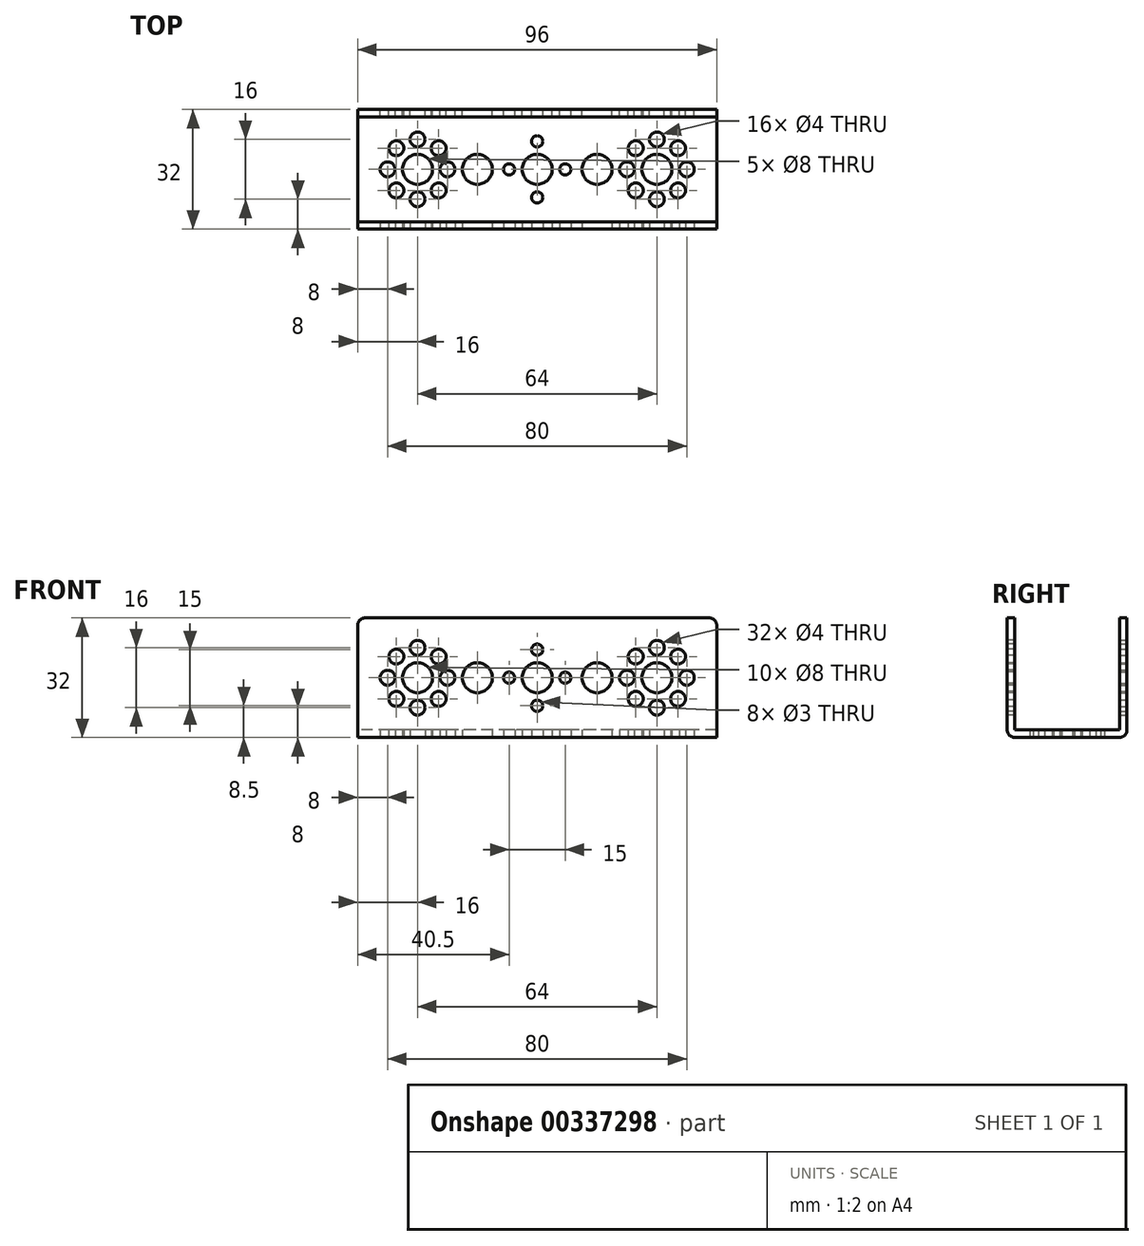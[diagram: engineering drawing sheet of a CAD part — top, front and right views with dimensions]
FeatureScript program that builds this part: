
annotation { "Feature Type Name" : "Feature", "Feature Type Description" : "" }
export const myFeature = defineFeature(function(context is Context, id is Id, definition is map)
    precondition{}
    {
        {
            var Q0;
            Q0=qCreatedBy(makeId("Top.planeOp"),FACE);
            var sketch = newSketch(context, id + "F0", { "sketchPlane" : qUnion([Q0])});
            skLineSegment(sketch, "E0.bottom", {"start": v(48, 16) * mm, "end": v(-48, 16) * mm});
            skLineSegment(sketch, "E0.top", {"start": v(48, -16) * mm, "end": v(-48, -16) * mm});
            skLineSegment(sketch, "E0.left", {"start": v(48, 16) * mm, "end": v(48, -16) * mm});
            skLineSegment(sketch, "E0.right", {"start": v(-48, 16) * mm, "end": v(-48, -16) * mm});
            skPoint(sketch, "E0.middle", {"position": v(0, 0) * mm});
            skLineSegment(sketch, "E1", {"start": v(-32, 2.64) * mm, "end": v(-32, 0) * mm});
            skLineSegment(sketch, "E2", {"start": v(-32, 0) * mm, "end": v(-32, -2.64) * mm});
            skLineSegment(sketch, "E3", {"start": v(-43.39, 0) * mm, "end": v(-32, 0) * mm});
            skLineSegment(sketch, "E4", {"start": v(-32, 0) * mm, "end": v(-37.82, 0) * mm});
            skLineSegment(sketch, "E5", {"start": v(-32, 0) * mm, "end": v(-30.72, 1.28) * mm});
            skLineSegment(sketch, "E6", {"start": v(-32, 0) * mm, "end": v(-33.4, -1.4) * mm});
            skLineSegment(sketch, "E7", {"start": v(-32, 0) * mm, "end": v(-33.4, 1.4) * mm});
            skLineSegment(sketch, "E8", {"start": v(-32, 0) * mm, "end": v(-30.62, -1.38) * mm});
            skCircle(sketch, "E9", {"center": v(-32, 0) * mm, "radius": 4 * mm});
            skCircle(sketch, "E10", {"center": v(-37.66, 5.66) * mm, "radius": 2 * mm});
            skCircle(sketch, "E11", {"center": v(-32, 8) * mm, "radius": 2 * mm});
            skCircle(sketch, "E12", {"center": v(-26.34, 5.66) * mm, "radius": 2 * mm});
            skCircle(sketch, "E13", {"center": v(-24, 0) * mm, "radius": 2 * mm});
            skCircle(sketch, "E14", {"center": v(-40, 0) * mm, "radius": 2 * mm});
            skCircle(sketch, "E15", {"center": v(-37.66, -5.66) * mm, "radius": 2 * mm});
            skCircle(sketch, "E16", {"center": v(-32, -8) * mm, "radius": 2 * mm});
            skCircle(sketch, "E17", {"center": v(-26.34, -5.66) * mm, "radius": 2 * mm});
            skCircle(sketch, "E18", {"center": v(-16, 0) * mm, "radius": 4 * mm});
            skCircle(sketch, "E19", {"center": v(0, 0) * mm, "radius": 4 * mm});
            skCircle(sketch, "E20", {"center": v(0, 7.5) * mm, "radius": 1.5 * mm});
            skCircle(sketch, "E21", {"center": v(7.5, 0) * mm, "radius": 1.5 * mm});
            skCircle(sketch, "E22", {"center": v(0, -7.5) * mm, "radius": 1.5 * mm});
            skCircle(sketch, "E23", {"center": v(-7.5, 0) * mm, "radius": 1.5 * mm});
            skCircle(sketch, "E24.MirrorC", {"center": v(16, 0) * mm, "radius": 4 * mm});
            skCircle(sketch, "E25.MirrorC", {"center": v(26.34, 5.66) * mm, "radius": 2 * mm});
            skCircle(sketch, "E26.MirrorC", {"center": v(32, 8) * mm, "radius": 2 * mm});
            skCircle(sketch, "E27.MirrorC", {"center": v(37.66, 5.66) * mm, "radius": 2 * mm});
            skCircle(sketch, "E28.MirrorC", {"center": v(37.66, -5.66) * mm, "radius": 2 * mm});
            skCircle(sketch, "E29.MirrorC", {"center": v(32, -8) * mm, "radius": 2 * mm});
            skCircle(sketch, "E30.MirrorC", {"center": v(26.34, -5.66) * mm, "radius": 2 * mm});
            skCircle(sketch, "E31.MirrorC", {"center": v(24, 0) * mm, "radius": 2 * mm});
            skCircle(sketch, "E32.MirrorC", {"center": v(32, 0) * mm, "radius": 4 * mm});
            skCircle(sketch, "E33.MirrorC", {"center": v(40, 0) * mm, "radius": 2 * mm});
            skSolve(sketch);
        }
        {
            var Q0;
            Q0=sQuery(id+"F0.wireOp",EDGE,"E0.top");
            var Q1;
            Q1=qCreatedBy(makeId("Front.planeOp"),FACE);
            cPlane(context, id + "F1", {"entities" : qUnion([Q0, Q1]), "cplaneType" : CPlaneType.LINE_ANGLE, "offset" : 25.4 * mm, "angle" : 0 * degree, "width" : 152.4 * mm, "height" : 152.4 * mm});
        }
        {
            var Q0;
            Q0=sQuery(id+"F0.wireOp",EDGE,"E0.bottom");
            var Q1;
            Q1=qCreatedBy(makeId("Front.planeOp"),FACE);
            cPlane(context, id + "F2", {"entities" : qUnion([Q0, Q1]), "cplaneType" : CPlaneType.LINE_ANGLE, "offset" : 25.4 * mm, "angle" : 0 * degree, "width" : 152.4 * mm, "height" : 152.4 * mm});
        }
        {
            var Q0;
            Q0=qCreatedBy(id+"F2.planeOp",FACE);
            var sketch = newSketch(context, id + "F3", { "sketchPlane" : qUnion([Q0])});
            skLineSegment(sketch, "E34.bottom", {"start": v(-48, 0) * mm, "end": v(48, 0) * mm});
            skLineSegment(sketch, "E34.top", {"start": v(-48, 32) * mm, "end": v(48, 32) * mm});
            skLineSegment(sketch, "E34.left", {"start": v(-48, 0) * mm, "end": v(-48, 32) * mm});
            skLineSegment(sketch, "E34.right", {"start": v(48, 0) * mm, "end": v(48, 32) * mm});
            skLineSegment(sketch, "E35", {"start": v(-32, 18.64) * mm, "end": v(-32, 16) * mm});
            skLineSegment(sketch, "E36", {"start": v(-32, 16) * mm, "end": v(-32, 13.36) * mm});
            skLineSegment(sketch, "E37", {"start": v(-45.1, 16) * mm, "end": v(-32, 16) * mm});
            skLineSegment(sketch, "E38", {"start": v(-32, 16) * mm, "end": v(-39.54, 16) * mm});
            skLineSegment(sketch, "E39", {"start": v(-32, 16) * mm, "end": v(-30.72, 17.28) * mm});
            skLineSegment(sketch, "E40", {"start": v(-32, 16) * mm, "end": v(-33.4, 14.6) * mm});
            skLineSegment(sketch, "E41", {"start": v(-32, 16) * mm, "end": v(-33.4, 17.4) * mm});
            skLineSegment(sketch, "E42", {"start": v(-32, 16) * mm, "end": v(-30.62, 14.62) * mm});
            skCircle(sketch, "E43", {"center": v(-32, 16) * mm, "radius": 4 * mm});
            skCircle(sketch, "E44", {"center": v(-37.66, 21.66) * mm, "radius": 2 * mm});
            skCircle(sketch, "E45", {"center": v(-32, 24) * mm, "radius": 2 * mm});
            skCircle(sketch, "E46", {"center": v(-26.34, 21.66) * mm, "radius": 2 * mm});
            skCircle(sketch, "E47", {"center": v(-24, 16) * mm, "radius": 2 * mm});
            skCircle(sketch, "E48", {"center": v(-40, 16) * mm, "radius": 2 * mm});
            skCircle(sketch, "E49", {"center": v(-37.66, 10.34) * mm, "radius": 2 * mm});
            skCircle(sketch, "E50", {"center": v(-32, 8) * mm, "radius": 2 * mm});
            skCircle(sketch, "E51", {"center": v(-26.34, 10.34) * mm, "radius": 2 * mm});
            skPoint(sketch, "E52", {"position": v(-48, 16) * mm});
            skCircle(sketch, "E53", {"center": v(0, 16) * mm, "radius": 4 * mm});
            skCircle(sketch, "E54", {"center": v(-16, 16) * mm, "radius": 4 * mm});
            skCircle(sketch, "E55", {"center": v(-7.5, 16) * mm, "radius": 1.5 * mm});
            skCircle(sketch, "E56", {"center": v(0, 23.5) * mm, "radius": 1.5 * mm});
            skCircle(sketch, "E57", {"center": v(7.5, 16) * mm, "radius": 1.5 * mm});
            skCircle(sketch, "E58", {"center": v(0, 8.5) * mm, "radius": 1.5 * mm});
            skCircle(sketch, "E59.MirrorC", {"center": v(16, 16) * mm, "radius": 4 * mm});
            skCircle(sketch, "E60.MirrorC", {"center": v(26.34, 21.66) * mm, "radius": 2 * mm});
            skCircle(sketch, "E61.MirrorC", {"center": v(32, 24) * mm, "radius": 2 * mm});
            skCircle(sketch, "E62.MirrorC", {"center": v(37.66, 21.66) * mm, "radius": 2 * mm});
            skCircle(sketch, "E63.MirrorC", {"center": v(40, 16) * mm, "radius": 2 * mm});
            skCircle(sketch, "E64.MirrorC", {"center": v(37.66, 10.34) * mm, "radius": 2 * mm});
            skCircle(sketch, "E65.MirrorC", {"center": v(32, 8) * mm, "radius": 2 * mm});
            skCircle(sketch, "E66.MirrorC", {"center": v(26.34, 10.34) * mm, "radius": 2 * mm});
            skCircle(sketch, "E67.MirrorC", {"center": v(24, 16) * mm, "radius": 2 * mm});
            skCircle(sketch, "E68.MirrorC", {"center": v(32, 16) * mm, "radius": 4 * mm});
            skSolve(sketch);
        }
        {
            var Q0;
            Q0=qCreatedBy(id+"F1.planeOp",FACE);
            var sketch = newSketch(context, id + "F4", { "sketchPlane" : qUnion([Q0])});
            skLineSegment(sketch, "E69.bottom", {"start": v(48, 0) * mm, "end": v(-48, 0) * mm});
            skLineSegment(sketch, "E69.top", {"start": v(48, 32) * mm, "end": v(-48, 32) * mm});
            skLineSegment(sketch, "E69.left", {"start": v(48, 0) * mm, "end": v(48, 32) * mm});
            skLineSegment(sketch, "E69.right", {"start": v(-48, 0) * mm, "end": v(-48, 32) * mm});
            skLineSegment(sketch, "E70", {"start": v(-32, 18.64) * mm, "end": v(-32, 16) * mm});
            skLineSegment(sketch, "E71", {"start": v(-32, 16) * mm, "end": v(-32, 13.36) * mm});
            skLineSegment(sketch, "E72", {"start": v(-32, 16) * mm, "end": v(-39.54, 16) * mm});
            skLineSegment(sketch, "E73", {"start": v(-32, 16) * mm, "end": v(-30.72, 17.28) * mm});
            skLineSegment(sketch, "E74", {"start": v(-32, 16) * mm, "end": v(-33.4, 14.6) * mm});
            skLineSegment(sketch, "E75", {"start": v(-32, 16) * mm, "end": v(-33.4, 17.4) * mm});
            skLineSegment(sketch, "E76", {"start": v(-32, 16) * mm, "end": v(-30.62, 14.62) * mm});
            skCircle(sketch, "E77", {"center": v(-32, 16) * mm, "radius": 4 * mm});
            skCircle(sketch, "E78", {"center": v(-37.66, 21.66) * mm, "radius": 2 * mm});
            skCircle(sketch, "E79", {"center": v(-32, 24) * mm, "radius": 2 * mm});
            skCircle(sketch, "E80", {"center": v(-26.34, 21.66) * mm, "radius": 2 * mm});
            skCircle(sketch, "E81", {"center": v(-24, 16) * mm, "radius": 2 * mm});
            skCircle(sketch, "E82", {"center": v(-40, 16) * mm, "radius": 2 * mm});
            skCircle(sketch, "E83", {"center": v(-37.66, 10.34) * mm, "radius": 2 * mm});
            skCircle(sketch, "E84", {"center": v(-32, 8) * mm, "radius": 2 * mm});
            skCircle(sketch, "E85", {"center": v(-26.34, 10.34) * mm, "radius": 2 * mm});
            skCircle(sketch, "E86", {"center": v(0, 16) * mm, "radius": 4 * mm});
            skCircle(sketch, "E87", {"center": v(-16, 16) * mm, "radius": 4 * mm});
            skCircle(sketch, "E88", {"center": v(-7.5, 16) * mm, "radius": 1.5 * mm});
            skCircle(sketch, "E89", {"center": v(0, 23.5) * mm, "radius": 1.5 * mm});
            skCircle(sketch, "E90", {"center": v(7.5, 16) * mm, "radius": 1.5 * mm});
            skCircle(sketch, "E91", {"center": v(0, 8.5) * mm, "radius": 1.5 * mm});
            skPoint(sketch, "E92", {"position": v(48, 16) * mm});
            skCircle(sketch, "E93.MirrorC", {"center": v(16, 16) * mm, "radius": 4 * mm});
            skCircle(sketch, "E94.MirrorC", {"center": v(24, 16) * mm, "radius": 2 * mm});
            skCircle(sketch, "E95.MirrorC", {"center": v(26.34, 21.66) * mm, "radius": 2 * mm});
            skCircle(sketch, "E96.MirrorC", {"center": v(32, 24) * mm, "radius": 2 * mm});
            skCircle(sketch, "E97.MirrorC", {"center": v(37.66, 21.66) * mm, "radius": 2 * mm});
            skCircle(sketch, "E98.MirrorC", {"center": v(40, 16) * mm, "radius": 2 * mm});
            skCircle(sketch, "E99.MirrorC", {"center": v(37.66, 10.34) * mm, "radius": 2 * mm});
            skCircle(sketch, "E100.MirrorC", {"center": v(32, 8) * mm, "radius": 2 * mm});
            skCircle(sketch, "E101.MirrorC", {"center": v(26.34, 10.34) * mm, "radius": 2 * mm});
            skCircle(sketch, "E102.MirrorC", {"center": v(32, 16) * mm, "radius": 4 * mm});
            skSolve(sketch);
        }
        {
            var Q0;
            Q0=makeQuery(id+"F0.imprint","IMPRINT",FACE,{"disambiguationData":[TD([[makeQuery(id+"F0.imprint","IMPRINT",EDGE,{"derivedFrom":sQuery(id+"F0.wireOp",EDGE,"E0.bottom")}),1.0]])]});
            extrude(context, id + "F5", {"entities" : qUnion([Q0]), "depth" : 2 * mm});
        }
        {
            var Q0;
            Q0=makeQuery(id+"F3.imprint","IMPRINT",FACE,{"disambiguationData":[TD([[makeQuery(id+"F3.imprint","IMPRINT",EDGE,{"derivedFrom":sQuery(id+"F3.wireOp",EDGE,"E34.bottom")}),1.0]])]});
            extrude(context, id + "F6", {"entities" : qUnion([Q0]), "operationType" : NewBodyOperationType.ADD, "oppositeDirection" : true, "depth" : 2 * mm});
        }
        {
            var Q0;
            Q0=makeQuery(id+"F4.imprint","IMPRINT",FACE,{"disambiguationData":[TD([[makeQuery(id+"F4.imprint","IMPRINT",EDGE,{"derivedFrom":sQuery(id+"F4.wireOp",EDGE,"E69.bottom")}),-1.0]])]});
            extrude(context, id + "F7", {"entities" : qUnion([Q0]), "operationType" : NewBodyOperationType.ADD, "depth" : 2 * mm});
        }
        {
            var Q0;
            Q0=makeQuery(id+"F5.opExtrude","CAP_EDGE",EDGE,{"disambiguationData":[OSD([sQuery(id+"F0.wireOp",EDGE,"E0.bottom")])],"isStart":true});
            var Q1;
            Q1=makeQuery(id+"F6.opExtrude","SWEPT_EDGE",EDGE,{"disambiguationData":[OSD([sQuery(id+"F3.wireOp",EDGE,"E34.top"),sQuery(id+"F3.wireOp",EDGE,"E34.left")])]});
            var Q2;
            Q2=makeQuery(id+"F7.opExtrude","SWEPT_EDGE",EDGE,{"disambiguationData":[OSD([sQuery(id+"F4.wireOp",EDGE,"E69.top"),sQuery(id+"F4.wireOp",EDGE,"E69.right")])]});
            var Q3;
            Q3=makeQuery(id+"F5.opExtrude","CAP_EDGE",EDGE,{"disambiguationData":[OSD([sQuery(id+"F0.wireOp",EDGE,"E0.top")])],"isStart":true});
            var Q4;
            Q4=makeQuery(id+"F6.opExtrude","SWEPT_EDGE",EDGE,{"disambiguationData":[OSD([sQuery(id+"F3.wireOp",EDGE,"E34.top"),sQuery(id+"F3.wireOp",EDGE,"E34.right")])]});
            var Q5;
            Q5=makeQuery(id+"F7.opExtrude","SWEPT_EDGE",EDGE,{"disambiguationData":[OSD([sQuery(id+"F4.wireOp",EDGE,"E69.top"),sQuery(id+"F4.wireOp",EDGE,"E69.left")])]});
            fillet(context, id + "F8", {"entities" : qUnion([Q0, Q1, Q2, Q3, Q4, Q5]), "radius" : 2 * mm, "tangentPropagation" : true, "allowEdgeOverflow" : false});
        }
    });
